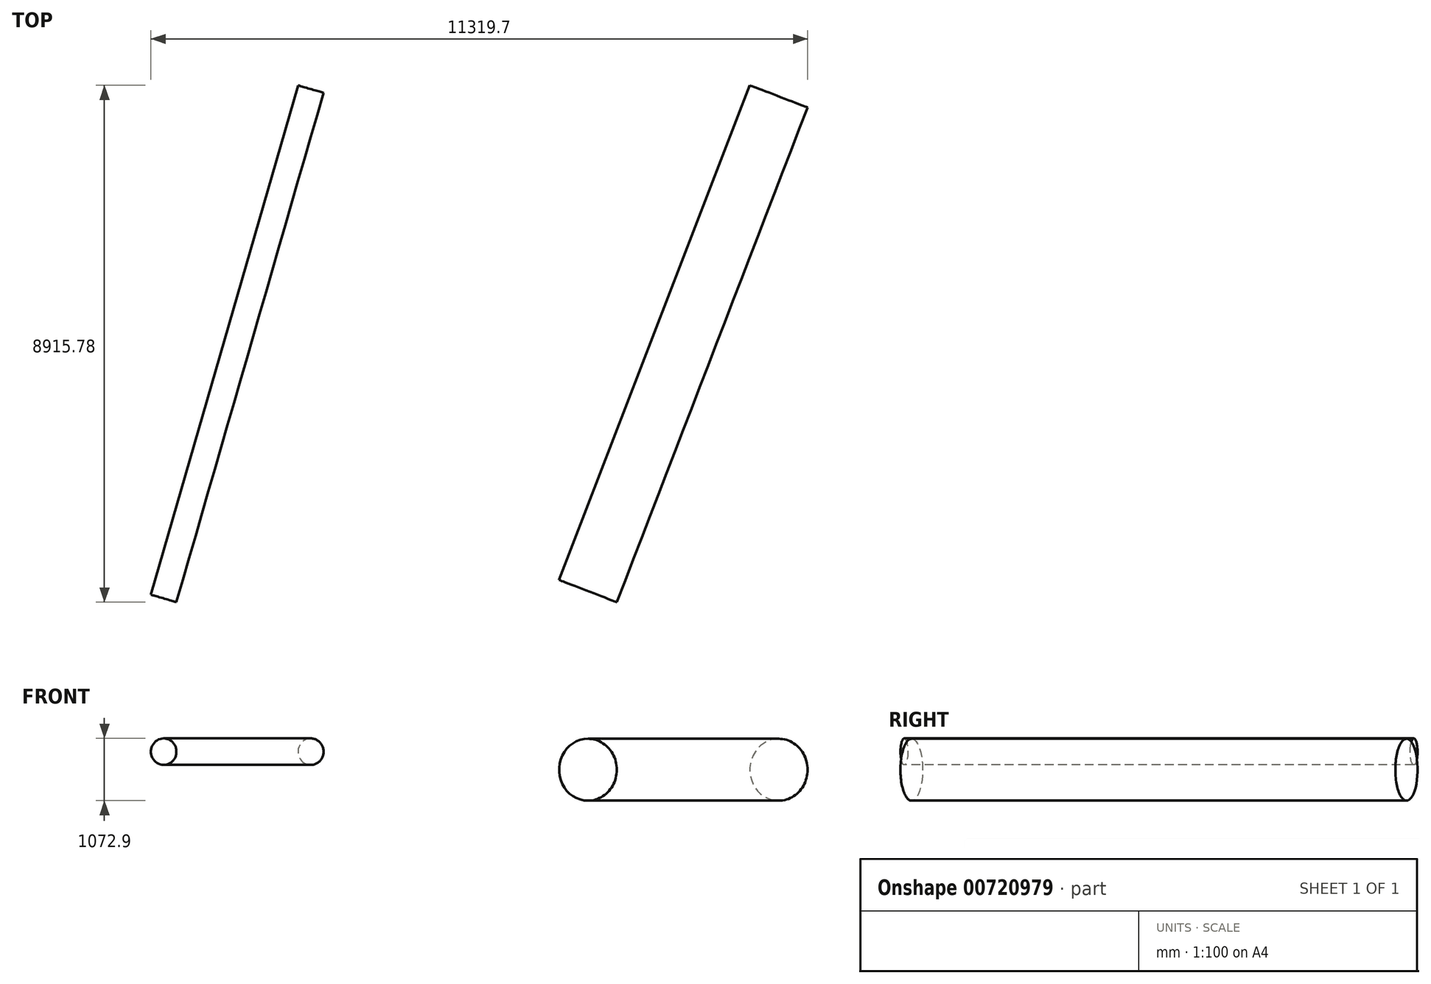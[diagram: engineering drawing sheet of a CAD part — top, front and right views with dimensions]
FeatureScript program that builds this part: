
annotation { "Feature Type Name" : "Feature", "Feature Type Description" : "" }
export const myFeature = defineFeature(function(context is Context, id is Id, definition is map)
    precondition{}
    {
        {
            var Q0;
            Q0=qCreatedBy(makeId("Top.planeOp"),FACE);
            cPlane(context, id + "F0", {"entities" : qUnion([Q0]), "cplaneType" : CPlaneType.OFFSET, "offset" : 731.52 * mm, "width" : 152.4 * mm, "height" : 152.4 * mm});
        }
        {
            var Q0;
            Q0=qCreatedBy(makeId("Top.planeOp"),FACE);
            cPlane(context, id + "F1", {"entities" : qUnion([Q0]), "cplaneType" : CPlaneType.OFFSET, "offset" : 1042.42 * mm, "width" : 152.4 * mm, "height" : 152.4 * mm});
        }
        {
            var Q0;
            Q0=qCreatedBy(id+"F0.planeOp",FACE);
            var sketch = newSketch(context, id + "F2", { "sketchPlane" : qUnion([Q0])});
            skLineSegment(sketch, "E0", {"start": v(8007.01, 4392.68) * mm, "end": v(5471.25, -4392.68) * mm, "construction": true});
            skPoint(sketch, "E1", {"position": v(6739.13, 0) * mm});
            skLineSegment(sketch, "E2", {"start": v(0, 0) * mm, "end": v(14429.23, 0) * mm, "construction": true});
            skLineSegment(sketch, "E3", {"start": v(16073.65, 4266.04) * mm, "end": v(12784.82, -4266.04) * mm, "construction": true});
            skPoint(sketch, "E4", {"position": v(14429.23, 0) * mm});
            skPoint(sketch, "E5", {"position": v(31107.89, 341.38) * mm});
            skLineSegment(sketch, "E6", {"start": v(0, 0) * mm, "end": v(0, -9144) * mm, "construction": true});
            skSolve(sketch);
        }
        {
            var Q0;
            Q0=qCreatedBy(id+"F1.planeOp",FACE);
            var sketch = newSketch(context, id + "F3", { "sketchPlane" : qUnion([Q0])});
            skLineSegment(sketch, "E7.0", {"start": v(8007.01, 4392.68) * mm, "end": v(5471.25, -4392.68) * mm, "construction": true});
            skSolve(sketch);
        }
        {
            var Q0;
            Q0=sQuery(id+"F2.wireOp",EDGE,"E0");
            cPlane(context, id + "F4", {"entities" : qUnion([Q0]), "cplaneType" : CPlaneType.LINE_ANGLE, "offset" : 25.4 * mm, "angle" : 90 * degree, "width" : 152.4 * mm, "height" : 152.4 * mm});
        }
        {
            var Q0;
            Q0=qCreatedBy(id+"F4.planeOp",FACE);
            var sketch = newSketch(context, id + "F5", { "sketchPlane" : qUnion([Q0])});
            skLineSegment(sketch, "E8.bottom", {"start": v(-2703.14, 1042.42) * mm, "end": v(6440.86, 1042.42) * mm});
            skLineSegment(sketch, "E8.top", {"start": v(-2703.14, 1271.02) * mm, "end": v(6440.86, 1271.02) * mm});
            skLineSegment(sketch, "E8.left", {"start": v(-2703.14, 1042.42) * mm, "end": v(-2703.14, 1271.02) * mm});
            skLineSegment(sketch, "E8.right", {"start": v(6440.86, 1042.42) * mm, "end": v(6440.86, 1271.02) * mm});
            skSolve(sketch);
        }
        {
            var Q0;
            Q0=sQuery(id+"F2.wireOp",EDGE,"E3");
            cPlane(context, id + "F6", {"entities" : qUnion([Q0]), "cplaneType" : CPlaneType.LINE_ANGLE, "offset" : 25.4 * mm, "angle" : 90 * degree, "width" : 152.4 * mm, "height" : 152.4 * mm});
        }
        {
            var Q0;
            Q0=qCreatedBy(id+"F6.planeOp",FACE);
            var sketch = newSketch(context, id + "F7", { "sketchPlane" : qUnion([Q0])});
            skLineSegment(sketch, "E9.bottom", {"start": v(617.78, 731.52) * mm, "end": v(9761.78, 731.52) * mm});
            skLineSegment(sketch, "E9.top", {"start": v(617.78, 1264.92) * mm, "end": v(9761.78, 1264.92) * mm});
            skLineSegment(sketch, "E9.left", {"start": v(617.78, 731.52) * mm, "end": v(617.78, 1264.92) * mm});
            skLineSegment(sketch, "E9.right", {"start": v(9761.78, 731.52) * mm, "end": v(9761.78, 1264.92) * mm});
            skLineSegment(sketch, "E10.MirrorCS", {"start": v(617.78, 198.12) * mm, "end": v(9761.78, 198.12) * mm, "construction": true});
            skSolve(sketch);
        }
        {
            var Q0;
            Q0=makeQuery(id+"F7.imprint","IMPRINT",FACE,{"disambiguationData":[TD([[makeQuery(id+"F7.imprint","IMPRINT",EDGE,{"derivedFrom":sQuery(id+"F7.wireOp",EDGE,"E9.bottom")}),1.0]])]});
            var Q1;
            Q1=sQuery(id+"F7.wireOp",EDGE,"E9.bottom");
            revolve(context, id + "F8", {"surfaceOperationType" : NewSurfaceOperationType.NEW, "entities" : qUnion([Q0]), "axis" : qUnion([Q1]), "revolveType" : RevolveType.FULL});
        }
        {
            var Q0;
            Q0=makeQuery(id+"F5.imprint","IMPRINT",FACE,{"disambiguationData":[TD([[makeQuery(id+"F5.imprint","IMPRINT",EDGE,{"derivedFrom":sQuery(id+"F5.wireOp",EDGE,"E8.bottom")}),1.0]])]});
            var Q1;
            Q1=sQuery(id+"F5.wireOp",EDGE,"E8.bottom");
            revolve(context, id + "F9", {"surfaceOperationType" : NewSurfaceOperationType.NEW, "entities" : qUnion([Q0]), "axis" : qUnion([Q1]), "revolveType" : RevolveType.FULL});
        }
        {
            var Q0;
            Q0=sQuery(id+"F2.wireOp",VERTEX,"E5");
            var Q1;
            Q1=qCreatedBy(makeId("Right.planeOp"),FACE);
            cPlane(context, id + "F10", {"entities" : qUnion([Q0, Q1]), "cplaneType" : CPlaneType.PLANE_POINT, "offset" : 25.4 * mm, "width" : 152.4 * mm, "height" : 152.4 * mm});
        }
    });
